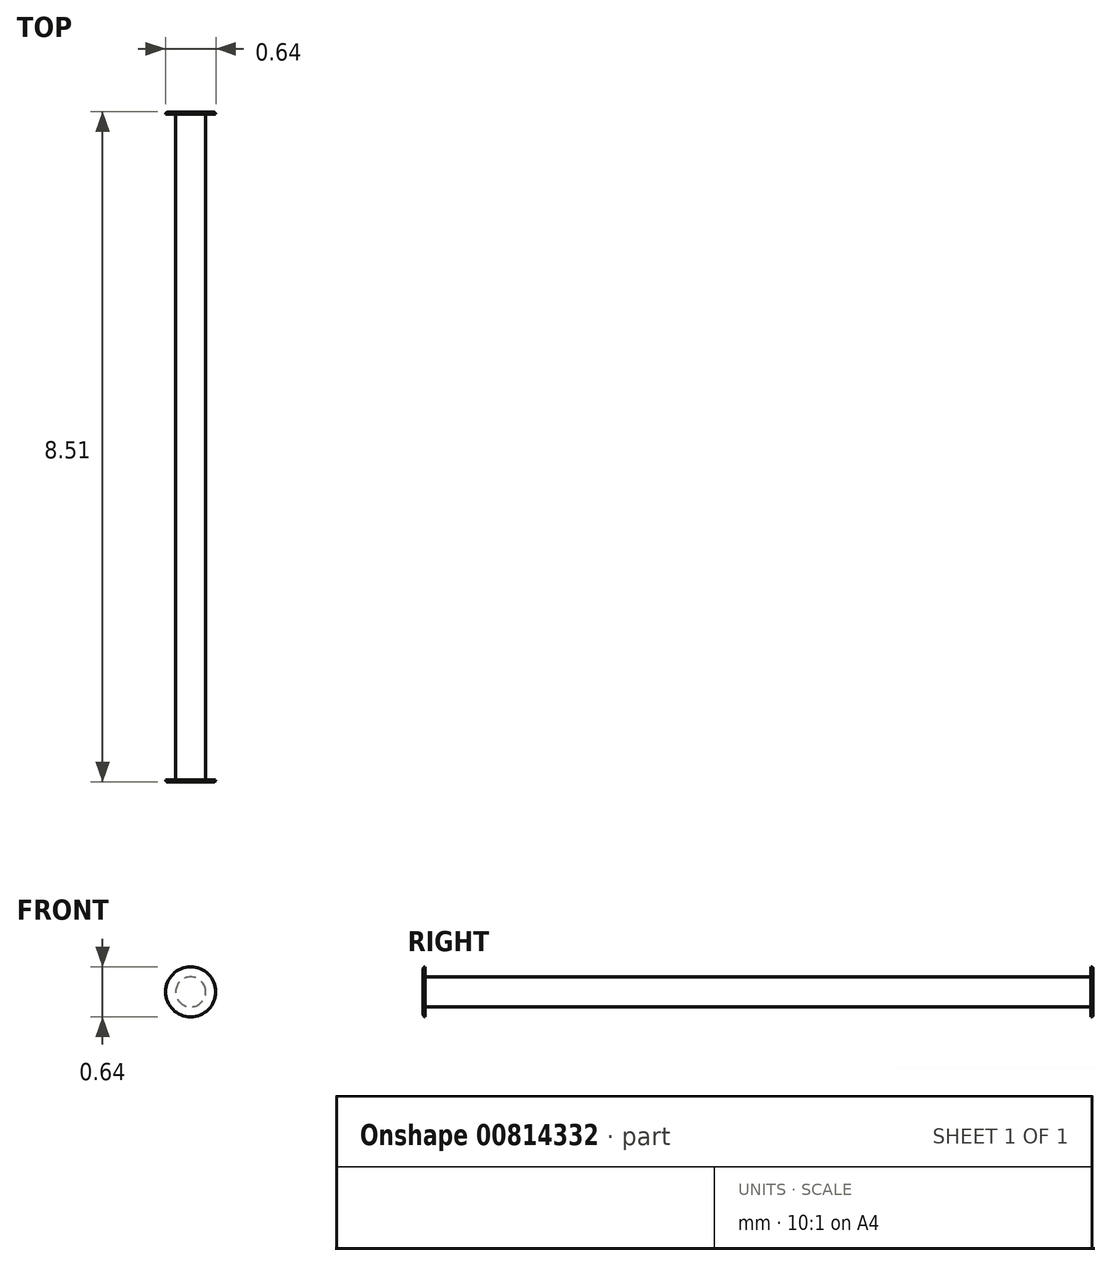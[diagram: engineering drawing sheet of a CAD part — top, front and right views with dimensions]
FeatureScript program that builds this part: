
annotation { "Feature Type Name" : "Feature", "Feature Type Description" : "" }
export const myFeature = defineFeature(function(context is Context, id is Id, definition is map)
    precondition{}
    {
        {
            var Q0;
            Q0=qCreatedBy(makeId("Front.planeOp"),FACE);
            var sketch = newSketch(context, id + "F0", { "sketchPlane" : qUnion([Q0])});
            skCircle(sketch, "E0", {"center": v(0, 0) * mm, "radius": 0.2 * mm});
            skSolve(sketch);
        }
        {
            var Q0;
            Q0 = qSketchRegion(id + "F0", true);
            extrude(context, id + "F1", {"entities" : qUnion([Q0]), "depth" : 8.46 * mm, "offsetDistance" : 25.4 * mm});
        }
        {
            var Q0;
            Q0=makeQuery(id+"F1.opExtrude","CAP_FACE",FACE,{"disambiguationData":[OSD([sQuery(id+"F0.wireOp",EDGE,"E0")])],"isStart":false});
            var sketch = newSketch(context, id + "F2", { "sketchPlane" : qUnion([Q0])});
            skCircle(sketch, "E1", {"center": v(0, 0) * mm, "radius": 0.32 * mm});
            skSolve(sketch);
        }
        {
            var Q0;
            Q0 = qSketchRegion(id + "F2", true);
            extrude(context, id + "F3", {"entities" : qUnion([Q0]), "operationType" : NewBodyOperationType.ADD, "depth" : 0.03 * mm, "offsetDistance" : 25.4 * mm});
        }
        {
            var Q0;
            Q0=makeQuery(id+"F1.opExtrude","CAP_FACE",FACE,{"disambiguationData":[OSD([sQuery(id+"F0.wireOp",EDGE,"E0")])],"isStart":true});
            var sketch = newSketch(context, id + "F4", { "sketchPlane" : qUnion([Q0])});
            skCircle(sketch, "E2", {"center": v(0, 0) * mm, "radius": 0.32 * mm});
            skSolve(sketch);
        }
        {
            var Q0;
            Q0 = qSketchRegion(id + "F4", true);
            extrude(context, id + "F5", {"entities" : qUnion([Q0]), "operationType" : NewBodyOperationType.ADD, "depth" : 0.03 * mm, "offsetDistance" : 25.4 * mm});
        }
        {
            var Q0;
            Q0=makeQuery(id+"F5.opExtrude","CAP_EDGE",EDGE,{"disambiguationData":[OSD([sQuery(id+"F4.wireOp",EDGE,"E2")])],"isStart":false});
            fillet(context, id + "F6", {"entities" : qUnion([Q0]), "radius" : 0.03 * mm, "tangentPropagation" : true, "allowEdgeOverflow" : false});
        }
        {
            var Q0;
            Q0=makeQuery(id+"F3.opExtrude","CAP_EDGE",EDGE,{"disambiguationData":[OSD([sQuery(id+"F2.wireOp",EDGE,"E1")])],"isStart":false});
            fillet(context, id + "F7", {"entities" : qUnion([Q0]), "radius" : 0.03 * mm, "tangentPropagation" : true, "allowEdgeOverflow" : false});
        }
    });
